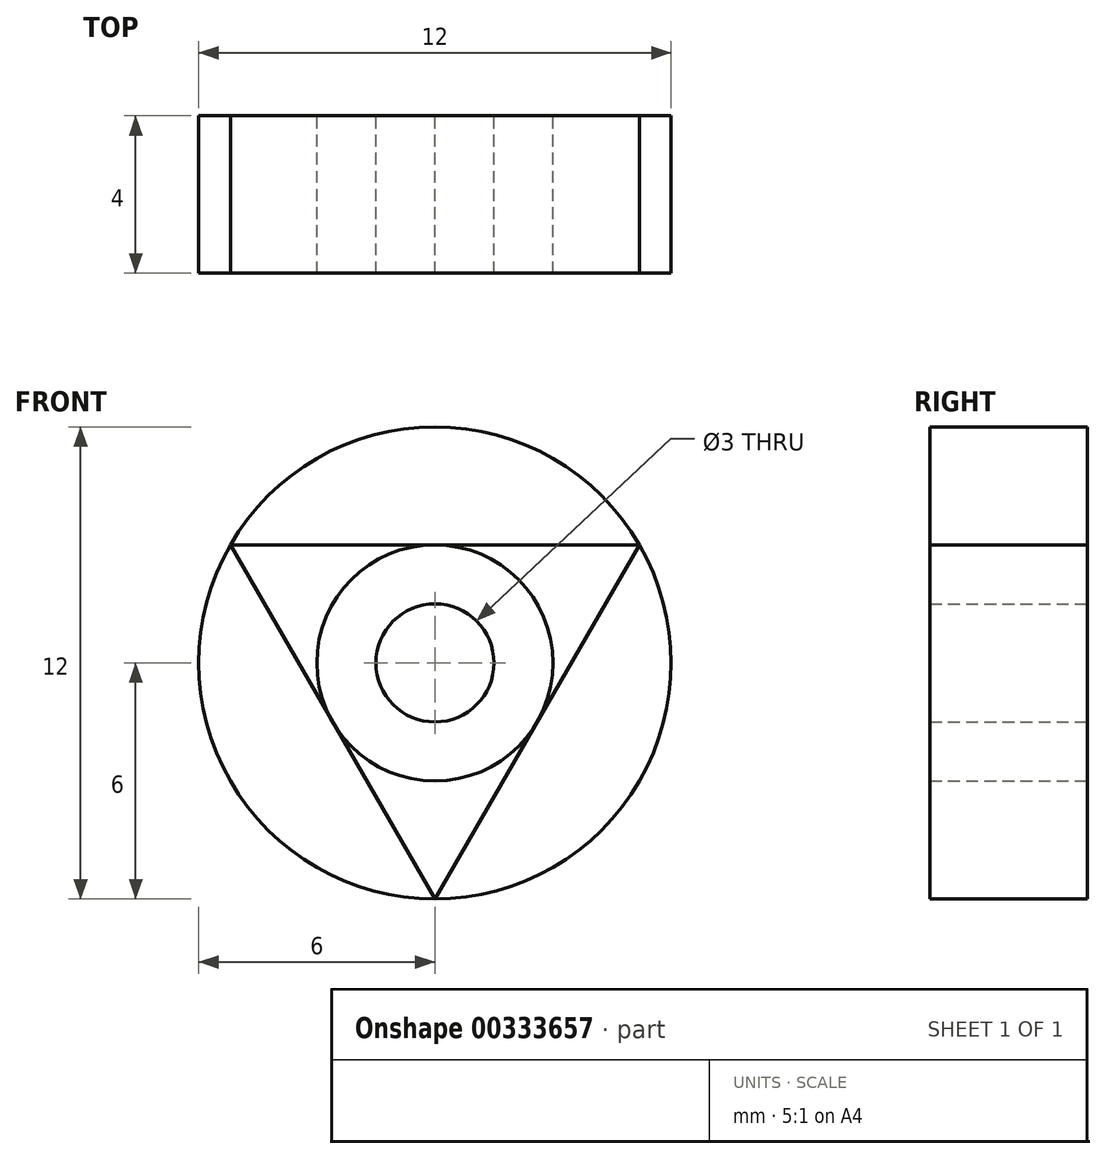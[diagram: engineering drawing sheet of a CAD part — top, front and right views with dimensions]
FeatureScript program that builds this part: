
annotation { "Feature Type Name" : "Feature", "Feature Type Description" : "" }
export const myFeature = defineFeature(function(context is Context, id is Id, definition is map)
    precondition{}
    {
        {
            var Q0;
            Q0=qCreatedBy(makeId("Front.planeOp"),FACE);
            var sketch = newSketch(context, id + "F0", { "sketchPlane" : qUnion([Q0])});
            skCircle(sketch, "E0", {"center": v(0, 0) * mm, "radius": 1.5 * mm});
            skCircle(sketch, "E1", {"center": v(0, 0) * mm, "radius": 3 * mm});
            skPoint(sketch, "E2.0.midPoint", {"position": v(-0.42, -2.97) * mm});
            skCircle(sketch, "E3.cCircle", {"center": v(0, 0) * mm, "radius": 3 * mm, "construction": true});
            skLineSegment(sketch, "E3.0", {"start": v(5.2, 3) * mm, "end": v(0, -6) * mm});
            skLineSegment(sketch, "E3.1", {"start": v(0, -6) * mm, "end": v(-5.2, 3) * mm});
            skLineSegment(sketch, "E3.2", {"start": v(-5.2, 3) * mm, "end": v(5.2, 3) * mm});
            skPoint(sketch, "E3.0.midPoint", {"position": v(2.6, -1.5) * mm});
            skCircle(sketch, "E4", {"center": v(0, 0) * mm, "radius": 6 * mm});
            skSolve(sketch);
        }
        {
            var Q0;
            {var subQ1=sQuery(id+"F0.wireOp",EDGE,"E3.2");var subQ3=makeQuery(id+"F0.imprint","INTERSECT",VERTEX,{"derivedFrom":[sQuery(id+"F0.wireOp",EDGE,"E1"),subQ1]});Q0=makeQuery(id+"F0.imprint","IMPRINT",FACE,{"disambiguationData":[TD([[makeQuery(id+"F0.imprint","IMPRINT",EDGE,{"disambiguationData":[TD([[subQ3,1.0]])],"derivedFrom":subQ1}),1.0]])]});}
            var Q1;
            {var subQ1=sQuery(id+"F0.wireOp",EDGE,"E3.0");var subQ3=makeQuery(id+"F0.imprint","INTERSECT",VERTEX,{"derivedFrom":[sQuery(id+"F0.wireOp",EDGE,"E1"),subQ1]});Q1=makeQuery(id+"F0.imprint","IMPRINT",FACE,{"disambiguationData":[TD([[makeQuery(id+"F0.imprint","IMPRINT",EDGE,{"disambiguationData":[TD([[subQ3,1.0]])],"derivedFrom":subQ1}),1.0]])]});}
            var Q2;
            {var subQ1=sQuery(id+"F0.wireOp",EDGE,"E3.1");var subQ3=makeQuery(id+"F0.imprint","INTERSECT",VERTEX,{"derivedFrom":[sQuery(id+"F0.wireOp",EDGE,"E1"),subQ1]});Q2=makeQuery(id+"F0.imprint","IMPRINT",FACE,{"disambiguationData":[TD([[makeQuery(id+"F0.imprint","IMPRINT",EDGE,{"disambiguationData":[TD([[subQ3,1.0]])],"derivedFrom":subQ1}),1.0]])]});}
            var Q3;
            Q3=makeQuery(id+"F0.imprint","IMPRINT",FACE,{"disambiguationData":[TD([[makeQuery(id+"F0.imprint","IMPRINT",EDGE,{"derivedFrom":sQuery(id+"F0.wireOp",EDGE,"E0")}),-1.0]])]});
            var Q4;
            Q4=sQuery(id+"F0.wireOp",EDGE,"E3.2");
            var Q5;
            Q5=sQuery(id+"F0.wireOp",EDGE,"E3.0");
            var Q6;
            Q6=sQuery(id+"F0.wireOp",EDGE,"E3.1");
            var Q7;
            Q7=sQuery(id+"F0.wireOp",EDGE,"E1");
            extrude(context, id + "F1", {"entities" : qUnion([Q0, Q1, Q2, Q3]), "surfaceEntities" : qUnion([Q4, Q5, Q6, Q7]), "depth" : 4 * mm});
        }
    });
